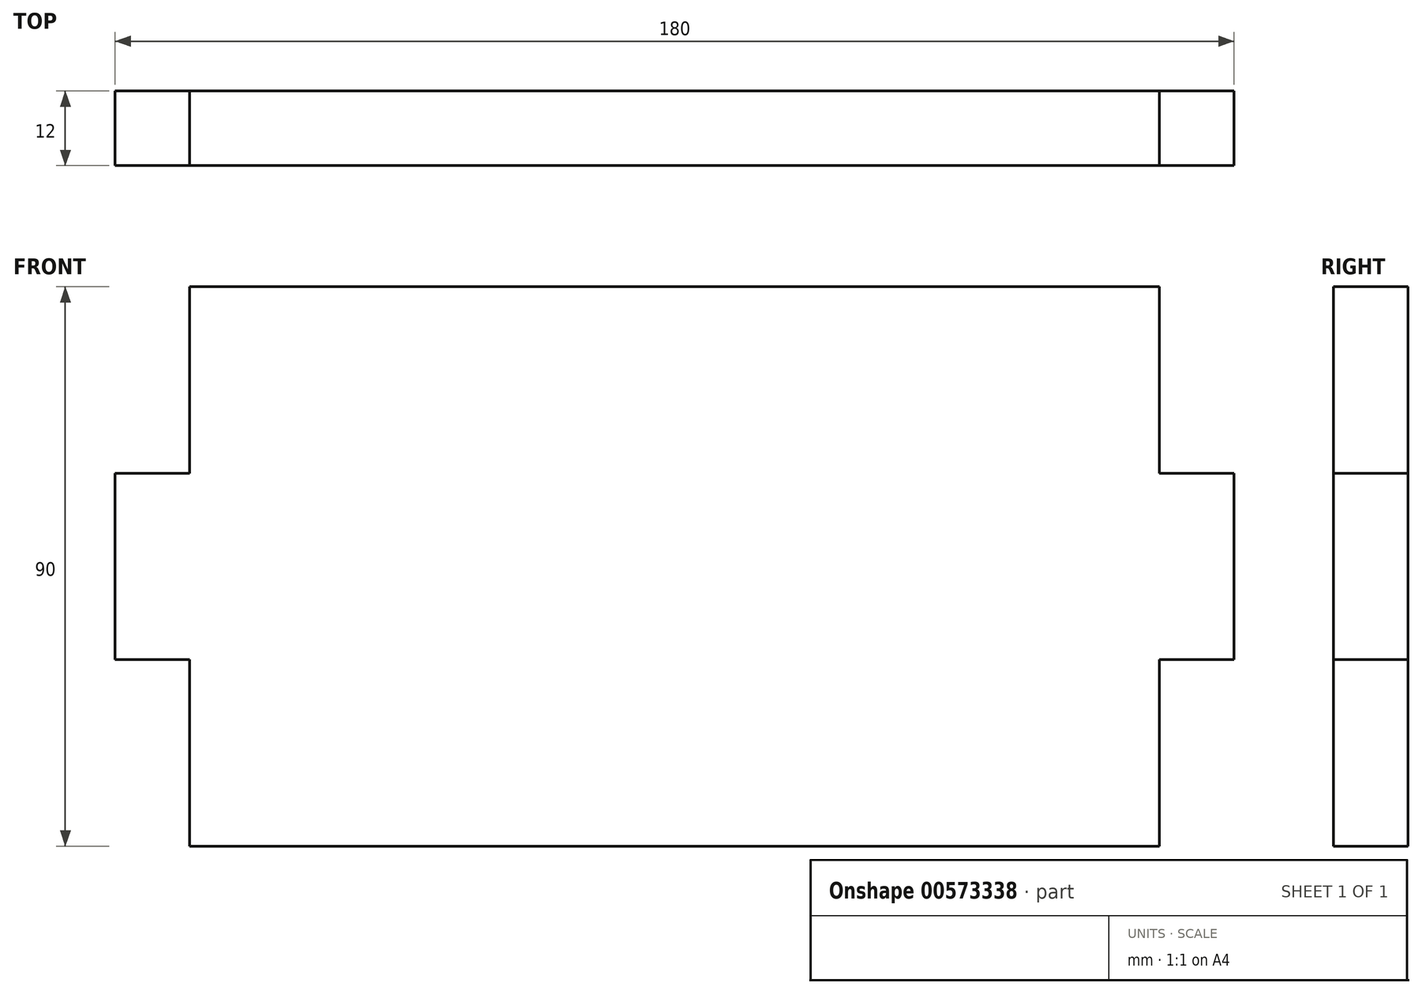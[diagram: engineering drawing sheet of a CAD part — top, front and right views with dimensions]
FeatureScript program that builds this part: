
annotation { "Feature Type Name" : "Feature", "Feature Type Description" : "" }
export const myFeature = defineFeature(function(context is Context, id is Id, definition is map)
    precondition{}
    {
        {
            var Q0;
            Q0=qCreatedBy(makeId("Front.planeOp"),FACE);
            var sketch = newSketch(context, id + "F0", { "sketchPlane" : qUnion([Q0])});
            skLineSegment(sketch, "E0", {"start": v(0, -21.16) * mm, "end": v(0, 8.84) * mm});
            skLineSegment(sketch, "E1", {"start": v(0, 8.84) * mm, "end": v(-12, 8.84) * mm});
            skLineSegment(sketch, "E2", {"start": v(-12, 8.84) * mm, "end": v(-12, 38.84) * mm});
            skLineSegment(sketch, "E3", {"start": v(-12, 38.84) * mm, "end": v(0, 38.84) * mm});
            skLineSegment(sketch, "E4", {"start": v(0, 38.84) * mm, "end": v(0, 68.84) * mm});
            skLineSegment(sketch, "E5", {"start": v(0, 68.84) * mm, "end": v(78, 68.84) * mm});
            skLineSegment(sketch, "E6", {"start": v(78, 68.84) * mm, "end": v(78, -21.16) * mm, "construction": true});
            skLineSegment(sketch, "E7", {"start": v(78, -21.16) * mm, "end": v(0, -21.16) * mm});
            skLineSegment(sketch, "E8.MirrorCS", {"start": v(78, -21.16) * mm, "end": v(156, -21.16) * mm});
            skLineSegment(sketch, "E9.MirrorCS", {"start": v(156, 68.84) * mm, "end": v(78, 68.84) * mm});
            skLineSegment(sketch, "E10.MirrorCS", {"start": v(156, 38.84) * mm, "end": v(156, 68.84) * mm});
            skLineSegment(sketch, "E11.MirrorCS", {"start": v(168, 38.84) * mm, "end": v(156, 38.84) * mm});
            skLineSegment(sketch, "E12.MirrorCS", {"start": v(168, 8.84) * mm, "end": v(168, 38.84) * mm});
            skLineSegment(sketch, "E13.MirrorCS", {"start": v(156, 8.84) * mm, "end": v(168, 8.84) * mm});
            skLineSegment(sketch, "E14.MirrorCS", {"start": v(156, -21.16) * mm, "end": v(156, 8.84) * mm});
            skSolve(sketch);
        }
        {
            var Q0;
            Q0 = qSketchRegion(id + "F0", true);
            extrude(context, id + "F1", {"entities" : qUnion([Q0]), "endBound" : BoundingType.SYMMETRIC, "depth" : 12 * mm, "offsetDistance" : 25 * mm});
        }
    });
